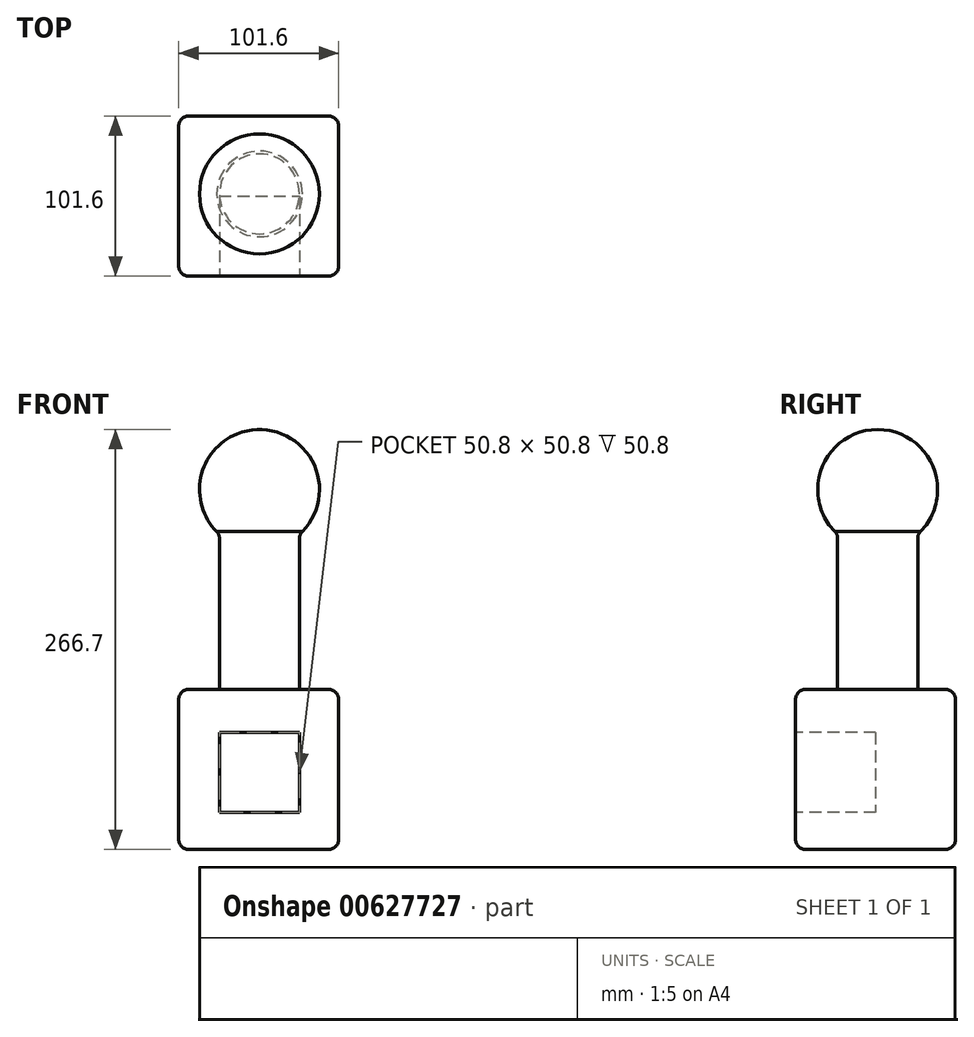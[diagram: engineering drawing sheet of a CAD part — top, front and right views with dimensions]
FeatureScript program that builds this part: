
annotation { "Feature Type Name" : "Feature", "Feature Type Description" : "" }
export const myFeature = defineFeature(function(context is Context, id is Id, definition is map)
    precondition{}
    {
        {
            var Q0;
            Q0=qCreatedBy(makeId("Top.planeOp"),FACE);
            var sketch = newSketch(context, id + "F0", { "sketchPlane" : qUnion([Q0])});
            skLineSegment(sketch, "E0.bottom", {"start": v(-51.33, 49.44) * mm, "end": v(50.27, 49.44) * mm});
            skLineSegment(sketch, "E0.top", {"start": v(-51.33, -52.16) * mm, "end": v(50.27, -52.16) * mm});
            skLineSegment(sketch, "E0.left", {"start": v(-51.33, 49.44) * mm, "end": v(-51.33, -52.16) * mm});
            skLineSegment(sketch, "E0.right", {"start": v(50.27, 49.44) * mm, "end": v(50.27, -52.16) * mm});
            skSolve(sketch);
        }
        {
            var Q0;
            Q0=makeQuery(id+"F0.imprint","IMPRINT",FACE,{"disambiguationData":[TD([[makeQuery(id+"F0.imprint","IMPRINT",EDGE,{"derivedFrom":sQuery(id+"F0.wireOp",EDGE,"E0.bottom")}),-1.0]])]});
            extrude(context, id + "F1", {"entities" : qUnion([Q0]), "depth" : 101.6 * mm, "offsetDistance" : 25.4 * mm});
        }
        {
            var Q0;
            Q0=makeQuery(id+"F1.opExtrude","CAP_FACE",FACE,{"disambiguationData":[OSD([sQuery(id+"F0.wireOp",EDGE,"E0.bottom"),sQuery(id+"F0.wireOp",EDGE,"E0.top"),sQuery(id+"F0.wireOp",EDGE,"E0.left"),sQuery(id+"F0.wireOp",EDGE,"E0.right")])],"isStart":false});
            var sketch = newSketch(context, id + "F2", { "sketchPlane" : qUnion([Q0])});
            skCircle(sketch, "E1", {"center": v(0, 0) * mm, "radius": 25.4 * mm});
            skSolve(sketch);
        }
        {
            var Q0;
            Q0 = qSketchRegion(id + "F2", true);
            extrude(context, id + "F3", {"entities" : qUnion([Q0]), "operationType" : NewBodyOperationType.ADD, "depth" : 25.4 * mm, "offsetDistance" : 25.4 * mm});
        }
        {
            var Q0;
            Q0=makeQuery(id+"F3.opExtrude","CAP_FACE",FACE,{"disambiguationData":[OSD([sQuery(id+"F2.wireOp",EDGE,"E1")])],"isStart":false});
            extrude(context, id + "F4", {"entities" : qUnion([Q0]), "operationType" : NewBodyOperationType.ADD, "depth" : 101.6 * mm, "offsetDistance" : 25.4 * mm});
        }
        {
            var Q0;
            Q0=makeQuery(id+"F4.opExtrude","CAP_FACE",FACE,{"disambiguationData":[OSD([sQuery(id+"F2.wireOp",EDGE,"E1")])],"isStart":false});
            var sketch = newSketch(context, id + "F5", { "sketchPlane" : qUnion([Q0])});
            skArc(sketch, "E2", {"start": v(0, -38.1) * mm, "mid": v(38.1, 0) * mm, "end": v(0, 38.1) * mm});
            skLineSegment(sketch, "E3", {"start": v(0, 38.1) * mm, "end": v(0, -38.1) * mm});
            skSolve(sketch);
        }
        {
            var Q0;
            {var subQ0=sQuery(id+"F5.wireOp",EDGE,"E2");Q0=makeQuery(id+"F5.imprint","IMPRINT",FACE,{"disambiguationData":[TD([[makeQuery(id+"F5.imprint","IMPRINT",EDGE,{"derivedFrom":subQ0}),1.0]])]});}
            var Q1;
            {var subQ0=sQuery(id+"F5.wireOp",EDGE,"E3");var subQ1=makeQuery(id+"F4.opExtrude","CAP_EDGE",EDGE,{"disambiguationData":[OSD([sQuery(id+"F2.wireOp",EDGE,"E1")])],"isStart":false});var subQ2=makeQuery(id+"F5.imprint","INTERSECT",VERTEX,{"disambiguationData":[OD(0.0)],"derivedFrom":[subQ1,subQ0]});Q1=makeQuery(id+"F5.imprint","IMPRINT",FACE,{"disambiguationData":[TD([[makeQuery(id+"F5.imprint","IMPRINT",EDGE,{"disambiguationData":[TD([[subQ2,-1.0]])],"derivedFrom":subQ0}),1.0]])]});}
            var Q2;
            Q2=sQuery(id+"F5.wireOp",EDGE,"E3");
            revolve(context, id + "F6", {"operationType" : NewBodyOperationType.ADD, "entities" : qUnion([Q0, Q1]), "axis" : qUnion([Q2]), "revolveType" : RevolveType.FULL});
        }
        {
            var Q0;
            Q0=makeQuery(id+"F1.opExtrude","SWEPT_FACE",FACE,{"disambiguationData":[OSD([sQuery(id+"F0.wireOp",EDGE,"E0.top")])]});
            var sketch = newSketch(context, id + "F7", { "sketchPlane" : qUnion([Q0])});
            skLineSegment(sketch, "E4.bottom", {"start": v(-25.4, 74.31) * mm, "end": v(25.4, 74.31) * mm});
            skLineSegment(sketch, "E4.top", {"start": v(-25.4, 23.51) * mm, "end": v(25.4, 23.51) * mm});
            skLineSegment(sketch, "E4.left", {"start": v(-25.4, 74.31) * mm, "end": v(-25.4, 23.51) * mm});
            skLineSegment(sketch, "E4.right", {"start": v(25.4, 74.31) * mm, "end": v(25.4, 23.51) * mm});
            skPoint(sketch, "E4.middle", {"position": v(0, 48.91) * mm});
            skSolve(sketch);
        }
        {
            var Q0;
            Q0=makeQuery(id+"F7.imprint","IMPRINT",FACE,{"disambiguationData":[TD([[makeQuery(id+"F7.imprint","IMPRINT",EDGE,{"derivedFrom":sQuery(id+"F7.wireOp",EDGE,"E4.bottom")}),-1.0]])]});
            extrude(context, id + "F8", {"entities" : qUnion([Q0]), "operationType" : NewBodyOperationType.REMOVE, "oppositeDirection" : true, "depth" : 50.8 * mm, "offsetDistance" : 25.4 * mm});
        }
        {
            var Q0;
            Q0=makeQuery(id+"F1.opExtrude","CAP_EDGE",EDGE,{"disambiguationData":[OSD([sQuery(id+"F0.wireOp",EDGE,"E0.right")])],"isStart":false});
            var Q1;
            Q1=makeQuery(id+"F1.opExtrude","CAP_EDGE",EDGE,{"disambiguationData":[OSD([sQuery(id+"F0.wireOp",EDGE,"E0.right")])],"isStart":true});
            var Q2;
            Q2=makeQuery(id+"F1.opExtrude","SWEPT_EDGE",EDGE,{"disambiguationData":[OSD([sQuery(id+"F0.wireOp",EDGE,"E0.top"),sQuery(id+"F0.wireOp",EDGE,"E0.right")])]});
            var Q3;
            Q3=makeQuery(id+"F1.opExtrude","SWEPT_EDGE",EDGE,{"disambiguationData":[OSD([sQuery(id+"F0.wireOp",EDGE,"E0.bottom"),sQuery(id+"F0.wireOp",EDGE,"E0.right")])]});
            var Q4;
            Q4=makeQuery(id+"F1.opExtrude","CAP_EDGE",EDGE,{"disambiguationData":[OSD([sQuery(id+"F0.wireOp",EDGE,"E0.top")])],"isStart":false});
            var Q5;
            Q5=makeQuery(id+"F1.opExtrude","SWEPT_EDGE",EDGE,{"disambiguationData":[OSD([sQuery(id+"F0.wireOp",EDGE,"E0.top"),sQuery(id+"F0.wireOp",EDGE,"E0.left")])]});
            var Q6;
            Q6=makeQuery(id+"F1.opExtrude","CAP_EDGE",EDGE,{"disambiguationData":[OSD([sQuery(id+"F0.wireOp",EDGE,"E0.top")])],"isStart":true});
            var Q7;
            Q7=makeQuery(id+"F1.opExtrude","CAP_EDGE",EDGE,{"disambiguationData":[OSD([sQuery(id+"F0.wireOp",EDGE,"E0.left")])],"isStart":true});
            var Q8;
            Q8=makeQuery(id+"F1.opExtrude","CAP_EDGE",EDGE,{"disambiguationData":[OSD([sQuery(id+"F0.wireOp",EDGE,"E0.bottom")])],"isStart":true});
            var Q9;
            Q9=makeQuery(id+"F1.opExtrude","CAP_EDGE",EDGE,{"disambiguationData":[OSD([sQuery(id+"F0.wireOp",EDGE,"E0.bottom")])],"isStart":false});
            var Q10;
            Q10=makeQuery(id+"F1.opExtrude","CAP_EDGE",EDGE,{"disambiguationData":[OSD([sQuery(id+"F0.wireOp",EDGE,"E0.left")])],"isStart":false});
            var Q11;
            Q11=makeQuery(id+"F1.opExtrude","SWEPT_EDGE",EDGE,{"disambiguationData":[OSD([sQuery(id+"F0.wireOp",EDGE,"E0.bottom"),sQuery(id+"F0.wireOp",EDGE,"E0.left")])]});
            var Q12;
            {var subQ0=sQuery(id+"F2.wireOp",EDGE,"E1");Q12=makeQuery(id+"F6.boolean.opBoolean","INTERSECT",EDGE,{"derivedFrom":[makeQuery(id+"F4.boolean.opBoolean","MERGE",FACE,{"derivedFrom":[makeQuery(id+"F3.opExtrude","SWEPT_FACE",FACE,{"disambiguationData":[OSD([subQ0])]}),makeQuery(id+"F4.opExtrude","SWEPT_FACE",FACE,{"disambiguationData":[OSD([subQ0])]})]}),makeQuery(id+"F6.opRevolve","SWEPT_FACE",FACE,{"disambiguationData":[OSD([sQuery(id+"F5.wireOp",EDGE,"E2")])]})]});}
            var Q13;
            Q13=makeQuery(id+"F3.opExtrude","CAP_EDGE",EDGE,{"disambiguationData":[OSD([sQuery(id+"F2.wireOp",EDGE,"E1")])],"isStart":true});
            fillet(context, id + "F9", {"entities" : qUnion([Q0, Q1, Q2, Q3, Q4, Q5, Q6, Q7, Q8, Q9, Q10, Q11, Q12, Q13]), "radius" : 6.35 * mm, "tangentPropagation" : true, "allowEdgeOverflow" : false});
        }
    });
